# Revit family: Bath_Combination-Grohe-Eurocube-19897000
name_source: partatom
category: Plumbing Fixtures
revit_build: Autodesk Revit 2014 (Build: 20130308_1515(x64)
units: mm (PartAtom-declared; Revit-internal decimal feet)

## types (1)
- 19897000
    Assembly Code = D2020300
    CW Connection = Yes
    CWFU = 3
    CalGreen Compliant = Yes
    Cold Water Connection Diameter = 1/2"
    Cold Water Connection Radius = 1/4"
    Default Elevation = 0"
    Description = Eurocube Four-hole Single-lever Bath Combination
    Finish = Metal-Grohe-000-Chrome
    Flow Rate = 6.9 gpm at 45 psi (26.1 L/min), 2.5 gpm (9.5 L/min) for Shower Hand
    HW Connection = Yes
    HWFU = 3
    Height = 9 15/16"
    Hot Water Connection Diameter = 1"
    Hot Water Connection Radius = 3/16"
    Installation Type = Deck-Mounted
    Length = 8 11/16"
    Manufacturer = Grohe
    Material = Metal-Grohe-000-Chrome
    Model = 19897000
    Price = Prices may vary. Please consult Manufacturer Representative for most up-to-date price list.
    Product Page URL = https://www.grohe.us
    Shipping Weight = 17.29 lb
    Tempered Water Connection Diameter = 1/2"
    URL = https://www.grohe.us
    Vent Connection = No
    WFU = 4
    Warranty Documentation Link = https://cdn.cloud.grohe.com
    Waste Connection = No
    Width = 19 3/4"
    cUPC Compliant = Yes

## geometry (parser evidence)
native form markers: Sweep x2
no freeform markers — native parametric forms only
